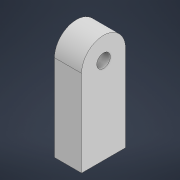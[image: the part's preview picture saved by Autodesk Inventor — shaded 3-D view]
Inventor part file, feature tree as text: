
AUTODESK INVENTOR PART (.ipt)
format: ipt  version: 2022 (Build 260153000, 153)  size: 129,024 bytes
history: native  units: mm
features: extrude x5, sketch x5, fillet x2
ambient origin geometry x8: Origin, YZ Plane, XZ Plane, XY Plane, X Axis, Y Axis, Z Axis, Center Point
bodies: Solid1 (feature_tree)
feature tree (12):
  extrude  "Extrusion1"  Depth=12.7mm
  extrude  "Extrusion6"  Depth=15.0mm TaperAngle=0.0deg
  extrude  "Extrusion11"  Depth=10.3mm
  fillet  "Fillet5"  Radius=4.8mm
  extrude  "Extrusion13"  Depth=10.3mm
  fillet  "Fillet6"  [1 undecoded]
  extrude  "Extrusion17"  Depth=0.872665mm
  sketch  "Sketch1"  dims[d1=25.4mm d2=12.7mm]
  sketch  "Sketch7"  dims[d3=45.0mm d4=0.0mm d23=15.0mm d24=0.0mm]
  sketch  "Sketch12"  dims[d44=9.216mm d45=0.0mm d46=10.3mm d50=4.8mm d51=0.0mm]
  sketch  "Sketch14"  dims[d52=10.3mm d65=6.35mm d66=0.0mm d67=0.0mm]
  sketch  "Sketch18"  dims[d5=0.5mm d6=0.872665mm d47=0.872665mm]
note: 1 required parameter value undecoded (feature->parameter linkage not recoverable at this tier; creation-order binding heuristic only, values carry confidence <= 0.55)
